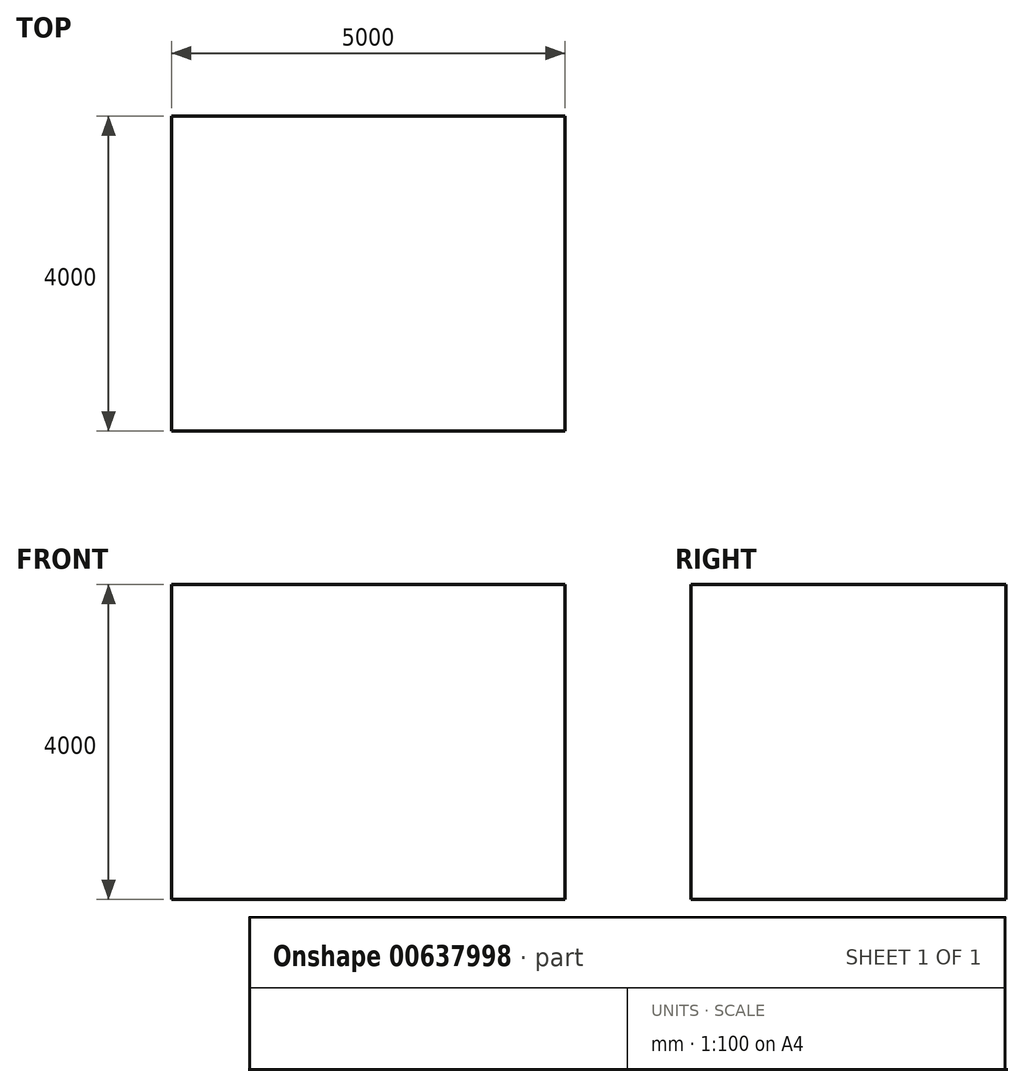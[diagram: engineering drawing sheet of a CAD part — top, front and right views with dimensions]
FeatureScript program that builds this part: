
annotation { "Feature Type Name" : "Feature", "Feature Type Description" : "" }
export const myFeature = defineFeature(function(context is Context, id is Id, definition is map)
    precondition{}
    {
        {
            var Q0;
            Q0=qCreatedBy(makeId("Top.planeOp"),FACE);
            var sketch = newSketch(context, id + "F0", { "sketchPlane" : qUnion([Q0])});
            skLineSegment(sketch, "E0.bottom", {"start": v(2500, -2000) * mm, "end": v(-2500, -2000) * mm});
            skLineSegment(sketch, "E0.top", {"start": v(2500, 2000) * mm, "end": v(-2500, 2000) * mm});
            skLineSegment(sketch, "E0.left", {"start": v(2500, -2000) * mm, "end": v(2500, 2000) * mm});
            skLineSegment(sketch, "E0.right", {"start": v(-2500, -2000) * mm, "end": v(-2500, 2000) * mm});
            skPoint(sketch, "E0.middle", {"position": v(0, 0) * mm});
            skSolve(sketch);
        }
        {
            var Q0;
            Q0=makeQuery(id+"F0.imprint","IMPRINT",FACE,{"disambiguationData":[TD([[makeQuery(id+"F0.imprint","IMPRINT",EDGE,{"derivedFrom":sQuery(id+"F0.wireOp",EDGE,"E0.bottom")}),-1.0]])]});
            extrude(context, id + "F1", {"entities" : qUnion([Q0]), "depth" : 4000 * mm, "offsetDistance" : 25.4 * mm});
        }
    });
